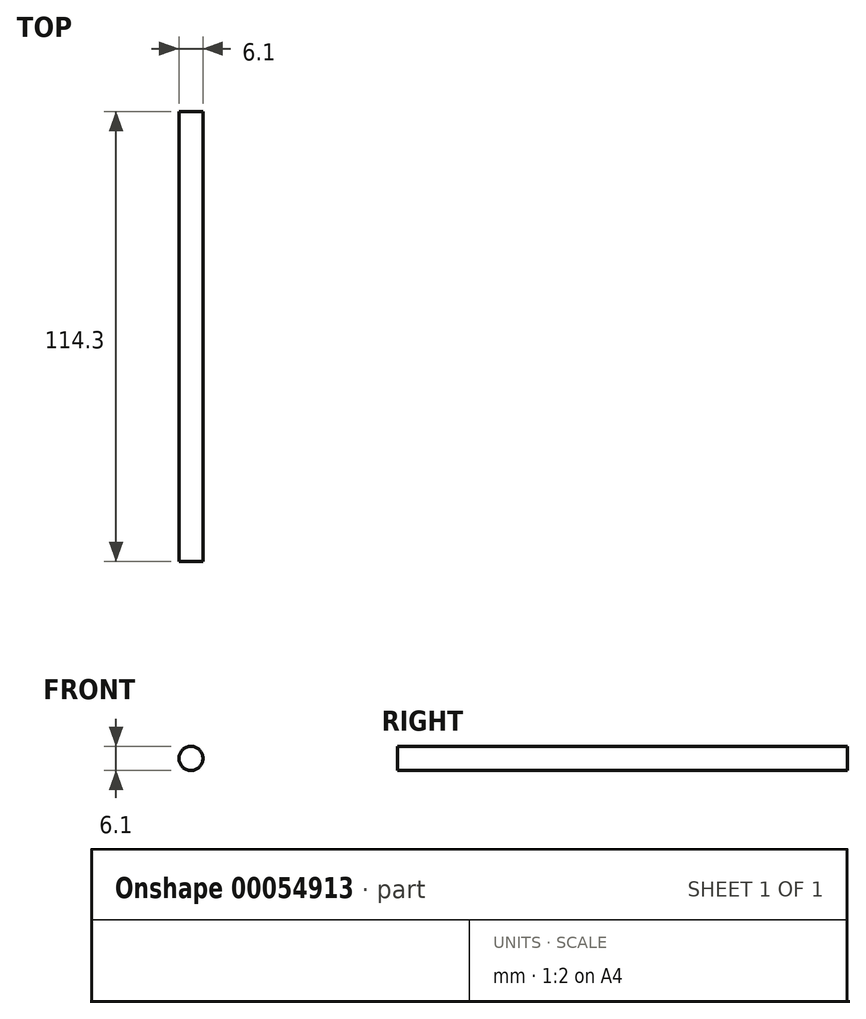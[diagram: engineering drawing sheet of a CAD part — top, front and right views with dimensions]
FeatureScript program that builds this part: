
annotation { "Feature Type Name" : "Feature", "Feature Type Description" : "" }
export const myFeature = defineFeature(function(context is Context, id is Id, definition is map)
    precondition{}
    {
        {
            var Q0;
            Q0=qCreatedBy(makeId("Front.planeOp"),FACE);
            var sketch = newSketch(context, id + "F0", { "sketchPlane" : qUnion([Q0])});
            skCircle(sketch, "E0", {"center": v(-54.67, -9.34) * mm, "radius": 3.05 * mm});
            skSolve(sketch);
        }
        {
            var Q0;
            Q0=makeQuery(id+"F0.imprint","IMPRINT",FACE,{"disambiguationData":[TD([[makeQuery(id+"F0.imprint","IMPRINT",EDGE,{"derivedFrom":sQuery(id+"F0.wireOp",EDGE,"E0")}),1.0]])]});
            extrude(context, id + "F1", {"entities" : qUnion([Q0]), "oppositeDirection" : true, "depth" : 114.3 * mm});
        }
    });
